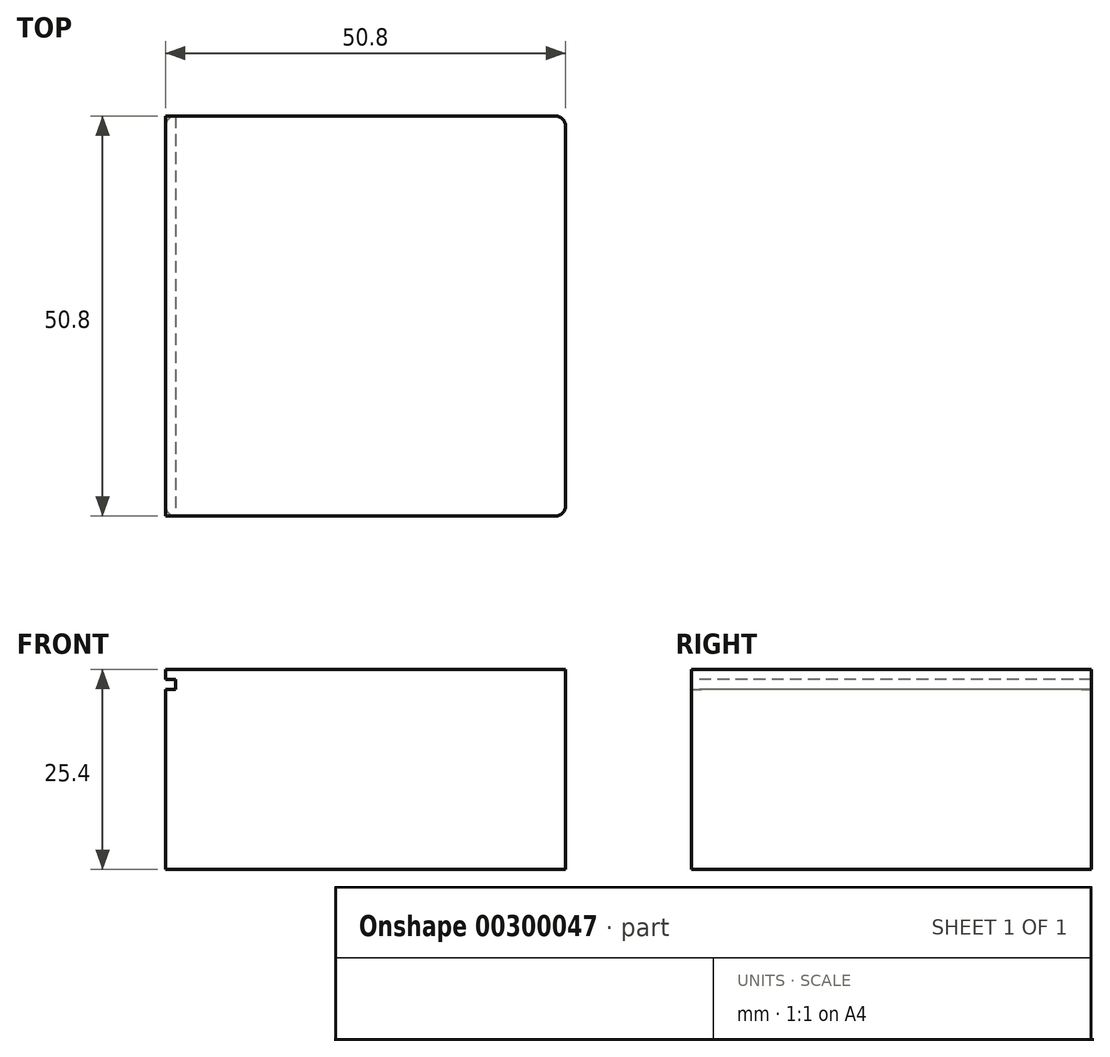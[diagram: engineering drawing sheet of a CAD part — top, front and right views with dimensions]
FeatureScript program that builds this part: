
annotation { "Feature Type Name" : "Feature", "Feature Type Description" : "" }
export const myFeature = defineFeature(function(context is Context, id is Id, definition is map)
    precondition{}
    {
        {
            var Q0;
            Q0=qCreatedBy(makeId("Top.planeOp"),FACE);
            var sketch = newSketch(context, id + "F0", { "sketchPlane" : qUnion([Q0])});
            skLineSegment(sketch, "E0.bottom", {"start": v(25.4, 25.4) * mm, "end": v(-25.4, 25.4) * mm});
            skLineSegment(sketch, "E0.top", {"start": v(25.4, -25.4) * mm, "end": v(-25.4, -25.4) * mm});
            skLineSegment(sketch, "E0.left", {"start": v(25.4, 25.4) * mm, "end": v(25.4, -25.4) * mm});
            skLineSegment(sketch, "E0.right", {"start": v(-25.4, 25.4) * mm, "end": v(-25.4, -25.4) * mm});
            skPoint(sketch, "E0.middle", {"position": v(0, 0) * mm});
            skSolve(sketch);
        }
        {
            var Q0;
            Q0 = qSketchRegion(id + "F0", true);
            extrude(context, id + "F1", {"entities" : qUnion([Q0]), "endBound" : BoundingType.SYMMETRIC, "depth" : 25.4 * mm});
        }
        {
            var Q0;
            Q0=makeQuery(id+"F1.opExtrude","SWEPT_FACE",FACE,{"disambiguationData":[OSD([sQuery(id+"F0.wireOp",EDGE,"E0.top")])]});
            var sketch = newSketch(context, id + "F2", { "sketchPlane" : qUnion([Q0])});
            skLineSegment(sketch, "E1.bottom", {"start": v(-25.4, 11.43) * mm, "end": v(-24.13, 11.43) * mm});
            skLineSegment(sketch, "E1.top", {"start": v(-25.4, 10.16) * mm, "end": v(-24.13, 10.16) * mm});
            skLineSegment(sketch, "E1.left", {"start": v(-25.4, 11.43) * mm, "end": v(-25.4, 10.16) * mm});
            skLineSegment(sketch, "E1.right", {"start": v(-24.13, 11.43) * mm, "end": v(-24.13, 10.16) * mm});
            skPoint(sketch, "E1.middle", {"position": v(-24.77, 10.8) * mm});
            skSolve(sketch);
        }
        {
            var Q0;
            Q0=qCreatedBy(makeId("Right.planeOp"),FACE);
            var sketch = newSketch(context, id + "F3", { "sketchPlane" : qUnion([Q0])});
            skLineSegment(sketch, "E2", {"start": v(0, 21.67) * mm, "end": v(0, -16.85) * mm, "construction": true});
            skSolve(sketch);
        }
        {
            var Q0;
            Q0 = qSketchRegion(id + "F2", true);
            extrude(context, id + "F4", {"entities" : qUnion([Q0]), "operationType" : NewBodyOperationType.REMOVE, "endBound" : BoundingType.THROUGH_ALL, "oppositeDirection" : true, "depth" : 25.4 * mm});
        }
        {
            var Q0;
            {var subQ0=sQuery(id+"F0.wireOp",EDGE,"E0.left");var subQ1=sQuery(id+"F0.wireOp",EDGE,"E0.top");var subQ2=sQuery(id+"F2.wireOp",EDGE,"E1.top");Q0=makeQuery(id+"FlJkfIp8fVTQSSJ_1.2.F4.boolean.opBoolean","SPLIT",EDGE,{"disambiguationData":[TD([makeQuery(id+"F4.boolean.opBoolean","COPY",FACE,{"derivedFrom":makeQuery(id+"F4.opExtrude","SWEPT_FACE",FACE,{"disambiguationData":[OSD([subQ2])]})})])],"derivedFrom":makeQuery(id+"F1.opExtrude","SWEPT_EDGE",EDGE,{"disambiguationData":[OSD([subQ1,subQ0])]})});}
            var Q1;
            {var subQ0=sQuery(id+"F0.wireOp",EDGE,"E0.left");var subQ1=sQuery(id+"F2.wireOp",EDGE,"E1.top");var subQ2=sQuery(id+"F0.wireOp",EDGE,"E0.bottom");Q1=makeQuery(id+"FlJkfIp8fVTQSSJ_1.1.F4.boolean.opBoolean","SPLIT",EDGE,{"disambiguationData":[TD([makeQuery(id+"F4.boolean.opBoolean","COPY",FACE,{"derivedFrom":makeQuery(id+"F4.opExtrude","SWEPT_FACE",FACE,{"disambiguationData":[OSD([subQ1])]})})])],"derivedFrom":makeQuery(id+"F1.opExtrude","SWEPT_EDGE",EDGE,{"disambiguationData":[OSD([subQ2,subQ0])]})});}
            var Q2;
            {var subQ0=sQuery(id+"F0.wireOp",EDGE,"E0.right");var subQ1=sQuery(id+"F0.wireOp",EDGE,"E0.top");Q2=makeQuery(id+"F4.boolean.opBoolean","SPLIT",EDGE,{"disambiguationData":[TD([makeQuery(id+"F4.opExtrude","SWEPT_FACE",FACE,{"disambiguationData":[OSD([sQuery(id+"F2.wireOp",EDGE,"E1.top")])]})])],"derivedFrom":makeQuery(id+"F1.opExtrude","SWEPT_EDGE",EDGE,{"disambiguationData":[OSD([subQ1,subQ0])]})});}
            var Q3;
            {var subQ0=sQuery(id+"F0.wireOp",EDGE,"E0.bottom");var subQ1=sQuery(id+"F0.wireOp",EDGE,"E0.right");Q3=makeQuery(id+"F4.boolean.opBoolean","SPLIT",EDGE,{"disambiguationData":[TD([makeQuery(id+"F4.opExtrude","SWEPT_FACE",FACE,{"disambiguationData":[OSD([sQuery(id+"F2.wireOp",EDGE,"E1.top")])]})])],"derivedFrom":makeQuery(id+"F1.opExtrude","SWEPT_EDGE",EDGE,{"disambiguationData":[OSD([subQ0,subQ1])]})});}
            fillet(context, id + "F5", {"entities" : qUnion([Q0, Q1, Q2, Q3]), "radius" : 1.27 * mm, "tangentPropagation" : true, "allowEdgeOverflow" : false});
        }
    });
